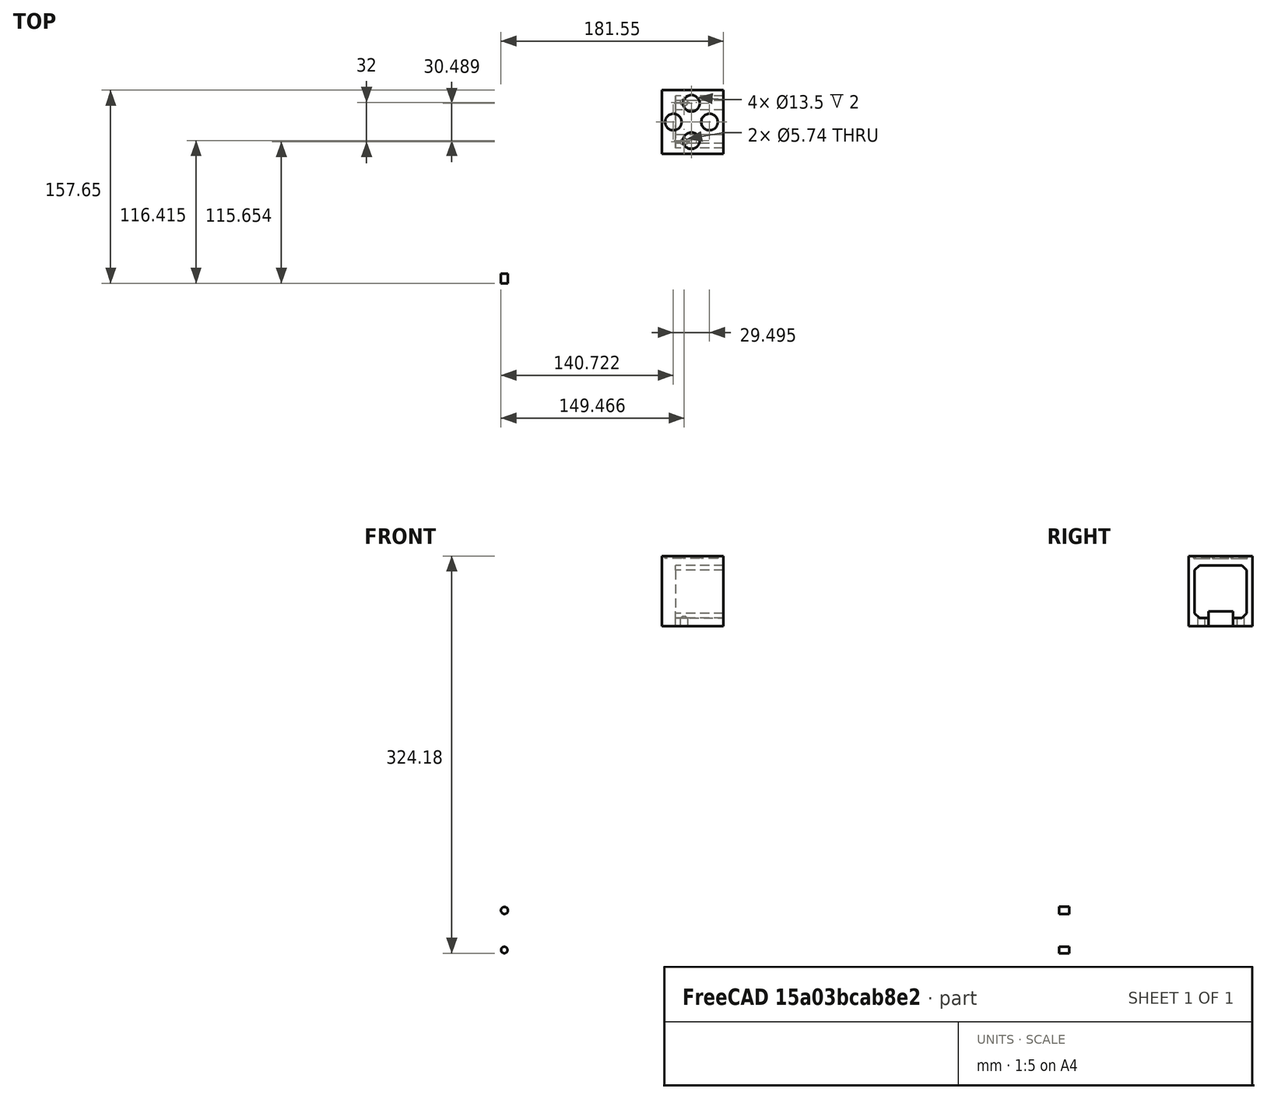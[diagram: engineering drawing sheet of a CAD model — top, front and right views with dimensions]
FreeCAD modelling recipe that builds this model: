
FCSTD DOCUMENT  (FreeCAD 0.16R6710 (Git))
Label: down holder
License: All rights reserved
LicenseURL: http://en.wikipedia.org/wiki/All_rights_reserved
objects: PartDesign::Pocket×4, Sketcher::SketchObject×2, Part::FeaturePython×1
note: 11 computed .brp shape members not serialized (recipe doc carries the construction recipe); baked Part::Feature solids carry a one-line shape summary decoded from their .brp

FEATURE [Part::FeaturePython] Extruder_Interface_April_12_01  # a2plus imported part (geometry in sourceFile) (typed FeaturePython)
  Placement = pos=(159.169,151.664,276.256) rot=(-1,0,0;1.5708rad)
  fixedPosition = false
  sourceFile = <userpath>/Downloads/D3D_Lo_3_April/Extruder_Interface_April_12.FCStd
  timeLastImport = 1.49216e+09
  updateColors = true
FEATURE [PartDesign::Pocket] Pocket
  Length = 100
  Placement = pos=(159.169,151.664,276.256) rot=(-1,0,0;1.5708rad)
  Type = 0
FEATURE [PartDesign::Pocket] Pocket001
  Length = 20
  Placement = pos=(159.169,151.664,276.256) rot=(-1,0,0;1.5708rad)
  Type = 0
FEATURE [Sketcher::SketchObject] Sketch
  Placement = pos=(159.163,151.664,248.249) rot=(0,1,0;3.14179rad)
  Support = -> Pocket001 [Face6]
  sketch-geometry (1):
    g0: Circle CenterX=-17.6278 CenterY=16.3303 CenterZ=0 NormalX=0 NormalY=0 NormalZ=1 Radius=2.9
  constraints (1):
    c: Radius(g0) = 2.9
FEATURE [PartDesign::Pocket] Pocket002
  Length = 8
  Placement = pos=(159.169,151.664,276.256) rot=(-1,0,0;1.5708rad)
  Sketch = -> Sketch
  Type = 0
FEATURE [Sketcher::SketchObject] Sketch001
  Placement = pos=(159.163,151.664,248.249) rot=(0,1,0;3.14179rad)
  Support = -> Pocket002 [Face6]
  sketch-geometry (1):
    g0: Circle CenterX=-17.4555 CenterY=-15.9623 CenterZ=0 NormalX=0 NormalY=0 NormalZ=1 Radius=2.62395
FEATURE [PartDesign::Pocket] Pocket003
  Length = 8
  Placement = pos=(159.169,151.664,276.256) rot=(-1,0,0;1.5708rad)
  Sketch = -> Sketch001
  Type = 0
